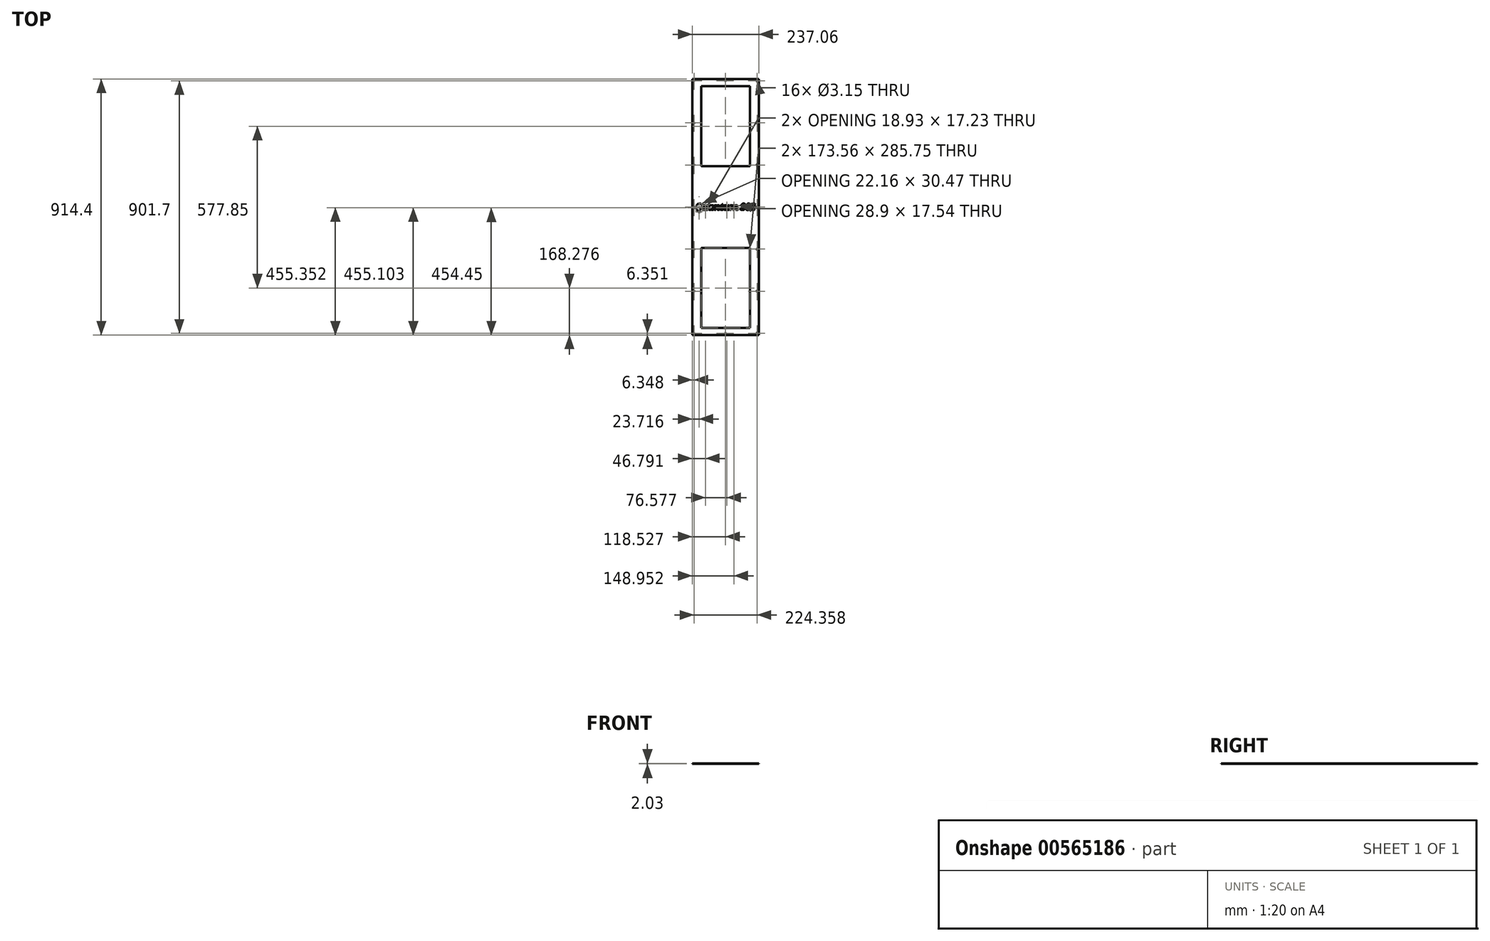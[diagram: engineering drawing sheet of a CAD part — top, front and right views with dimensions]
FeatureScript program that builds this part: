
annotation { "Feature Type Name" : "Feature", "Feature Type Description" : "" }
export const myFeature = defineFeature(function(context is Context, id is Id, definition is map)
    precondition{}
    {
        {
            var Q0;
            Q0=qCreatedBy(makeId("Top.planeOp"),FACE);
            var sketch = newSketch(context, id + "F0", { "sketchPlane" : qUnion([Q0])});
            skLineSegment(sketch, "E0.bottom", {"start": v(-468.83, 470.81) * mm, "end": v(-231.77, 470.81) * mm});
            skLineSegment(sketch, "E0.top", {"start": v(-468.83, -443.59) * mm, "end": v(-231.77, -443.59) * mm});
            skLineSegment(sketch, "E0.left", {"start": v(-468.83, 470.81) * mm, "end": v(-468.83, -443.59) * mm});
            skLineSegment(sketch, "E0.right", {"start": v(-231.77, 470.81) * mm, "end": v(-231.77, -443.59) * mm});
            skLineSegment(sketch, "E1.bottom", {"start": v(-437.08, 445.41) * mm, "end": v(-263.52, 445.41) * mm});
            skLineSegment(sketch, "E1.top", {"start": v(-437.08, 159.66) * mm, "end": v(-263.52, 159.66) * mm});
            skLineSegment(sketch, "E1.left", {"start": v(-437.08, 445.41) * mm, "end": v(-437.08, 159.66) * mm});
            skLineSegment(sketch, "E1.right", {"start": v(-263.52, 445.41) * mm, "end": v(-263.52, 159.66) * mm});
            skLineSegment(sketch, "E2.bottom", {"start": v(-437.08, -132.44) * mm, "end": v(-263.52, -132.44) * mm});
            skLineSegment(sketch, "E2.top", {"start": v(-437.08, -418.19) * mm, "end": v(-263.52, -418.19) * mm});
            skLineSegment(sketch, "E2.left", {"start": v(-437.08, -132.44) * mm, "end": v(-437.08, -418.19) * mm});
            skLineSegment(sketch, "E2.right", {"start": v(-263.52, -132.44) * mm, "end": v(-263.52, -418.19) * mm});
            skLineSegment(sketch, "E3", {"start": v(-468.83, 13.61) * mm, "end": v(-231.77, 13.61) * mm, "construction": true});
            skLineSegment(sketch, "E4", {"start": v(-350.3, 470.81) * mm, "end": v(-350.3, -443.59) * mm, "construction": true});
            skLineSegment(sketch, "E5.0", {"start": v(-462.48, 464.46) * mm, "end": v(-462.48, -437.24) * mm, "construction": true});
            skLineSegment(sketch, "E5.1", {"start": v(-462.48, 464.46) * mm, "end": v(-238.12, 464.46) * mm, "construction": true});
            skLineSegment(sketch, "E5.2", {"start": v(-238.12, 464.46) * mm, "end": v(-238.12, -437.24) * mm, "construction": true});
            skLineSegment(sketch, "E5.3", {"start": v(-462.48, -437.24) * mm, "end": v(-238.12, -437.24) * mm, "construction": true});
            skCircle(sketch, "E6", {"center": v(-462.48, 464.46) * mm, "radius": 1.57 * mm});
            skCircle(sketch, "E7", {"center": v(-462.48, -437.24) * mm, "radius": 1.57 * mm});
            skCircle(sketch, "E8", {"center": v(-238.12, -437.24) * mm, "radius": 1.57 * mm});
            skCircle(sketch, "E9", {"center": v(-238.12, 464.46) * mm, "radius": 1.57 * mm});
            skCircle(sketch, "E10", {"center": v(-350.3, 464.46) * mm, "radius": 1.57 * mm});
            skCircle(sketch, "E11", {"center": v(-350.3, -437.24) * mm, "radius": 1.57 * mm});
            skCircle(sketch, "E12", {"center": v(-462.48, 13.61) * mm, "radius": 1.57 * mm});
            skCircle(sketch, "E13", {"center": v(-238.12, 13.61) * mm, "radius": 1.57 * mm});
            skLineSegment(sketch, "E14.0", {"start": v(-468.83, 163.9) * mm, "end": v(-231.77, 163.9) * mm, "construction": true});
            skLineSegment(sketch, "E15.0", {"start": v(-468.83, 314.18) * mm, "end": v(-231.77, 314.18) * mm, "construction": true});
            skCircle(sketch, "E16", {"center": v(-462.48, 314.18) * mm, "radius": 1.57 * mm});
            skCircle(sketch, "E17", {"center": v(-462.48, 163.9) * mm, "radius": 1.57 * mm});
            skCircle(sketch, "E18", {"center": v(-238.12, 314.18) * mm, "radius": 1.57 * mm});
            skCircle(sketch, "E19", {"center": v(-238.12, 163.9) * mm, "radius": 1.57 * mm});
            skCircle(sketch, "E20.MirrorC", {"center": v(-462.48, -136.67) * mm, "radius": 1.57 * mm});
            skCircle(sketch, "E21.MirrorC", {"center": v(-238.12, -136.67) * mm, "radius": 1.57 * mm});
            skCircle(sketch, "E22.MirrorC", {"center": v(-238.12, -286.96) * mm, "radius": 1.57 * mm});
            skCircle(sketch, "E23.MirrorC", {"center": v(-462.48, -286.96) * mm, "radius": 1.57 * mm});
            skText(sketch, "E24", { "text": "Quantum 304", "fontName": "NotoSerif-BoldItalic.ttf"});
            const initialGuessF0  = {"E24": [-0.45815, 0.00321, 1, 0, 0.02272]};
            skSetInitialGuess(sketch, initialGuessF0);
            skSolve(sketch);
        }
        {
            var Q0;
            Q0=makeQuery(id+"F0.imprint","IMPRINT",FACE,{"disambiguationData":[TD([[makeQuery(id+"F0.imprint","IMPRINT",EDGE,{"derivedFrom":sQuery(id+"F0.wireOp",EDGE,"E0.bottom")}),-1.0]])]});
            extrude(context, id + "F1", {"entities" : qUnion([Q0]), "depth" : 2.03 * mm, "offsetDistance" : 25.4 * mm});
        }
    });
